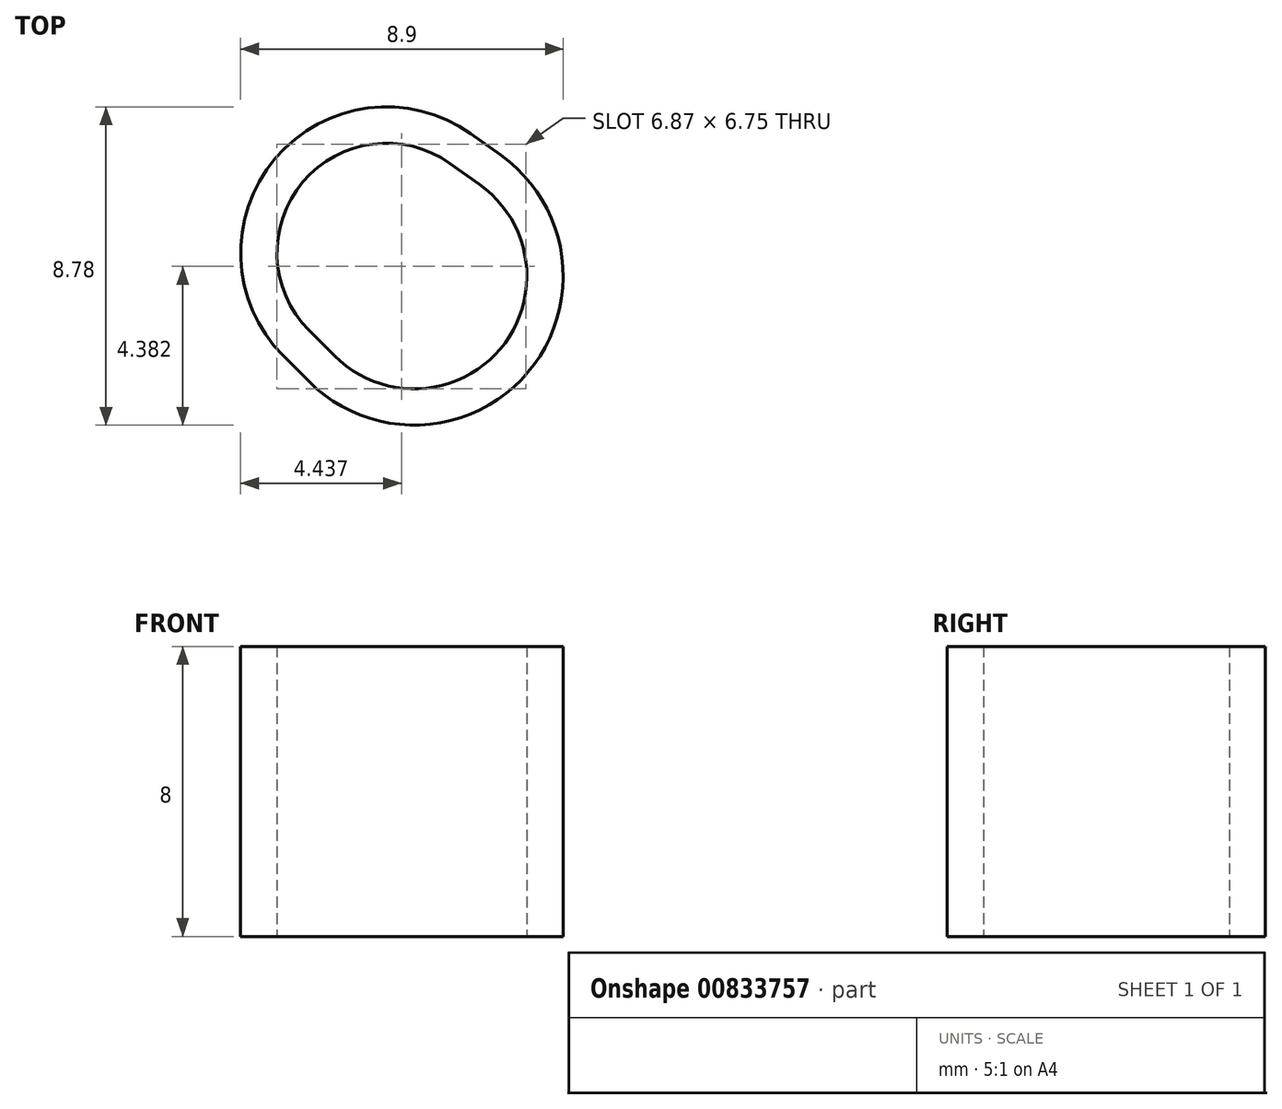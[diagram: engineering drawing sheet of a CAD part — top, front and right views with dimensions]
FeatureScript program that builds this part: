
annotation { "Feature Type Name" : "Feature", "Feature Type Description" : "" }
export const myFeature = defineFeature(function(context is Context, id is Id, definition is map)
    precondition{}
    {
        {
            var Q0;
            Q0=qCreatedBy(makeId("Top.planeOp"),FACE);
            var sketch = newSketch(context, id + "F0", { "sketchPlane" : qUnion([Q0])});
            skArc(sketch, "E0.MirrorCS", {"start": v(-79.18, 25.84) * mm, "mid": v(-83.24, 25.33) * mm, "end": v(-83.07, 21.24) * mm});
            skArc(sketch, "E1.0", {"start": v(-78.6, 26.66) * mm, "mid": v(-84, 25.98) * mm, "end": v(-83.77, 20.54) * mm});
            skLineSegment(sketch, "E2", {"start": v(-83.77, 20.54) * mm, "end": v(-83.07, 19.83) * mm});
            skLineSegment(sketch, "E3", {"start": v(-83.07, 21.24) * mm, "end": v(-82.36, 20.54) * mm});
            skLineSegment(sketch, "E4", {"start": v(-79.18, 25.84) * mm, "end": v(-78.36, 25.26) * mm});
            skLineSegment(sketch, "E5", {"start": v(-78.6, 26.66) * mm, "end": v(-77.78, 26.08) * mm});
            skArc(sketch, "E6", {"start": v(-82.36, 20.54) * mm, "mid": v(-77.79, 20.73) * mm, "end": v(-78.36, 25.26) * mm});
            skArc(sketch, "E7", {"start": v(-83.07, 19.83) * mm, "mid": v(-77.03, 20.08) * mm, "end": v(-77.78, 26.08) * mm});
            skSolve(sketch);
        }
        {
            var Q0;
            Q0=makeQuery(id+"F0.imprint","IMPRINT",FACE,{"disambiguationData":[TD([[makeQuery(id+"F0.imprint","IMPRINT",EDGE,{"derivedFrom":sQuery(id+"F0.wireOp",EDGE,"E0.MirrorCS")}),-1.0]])]});
            extrude(context, id + "F1", {"entities" : qUnion([Q0]), "depth" : 8 * mm, "offsetDistance" : 25 * mm});
        }
    });
